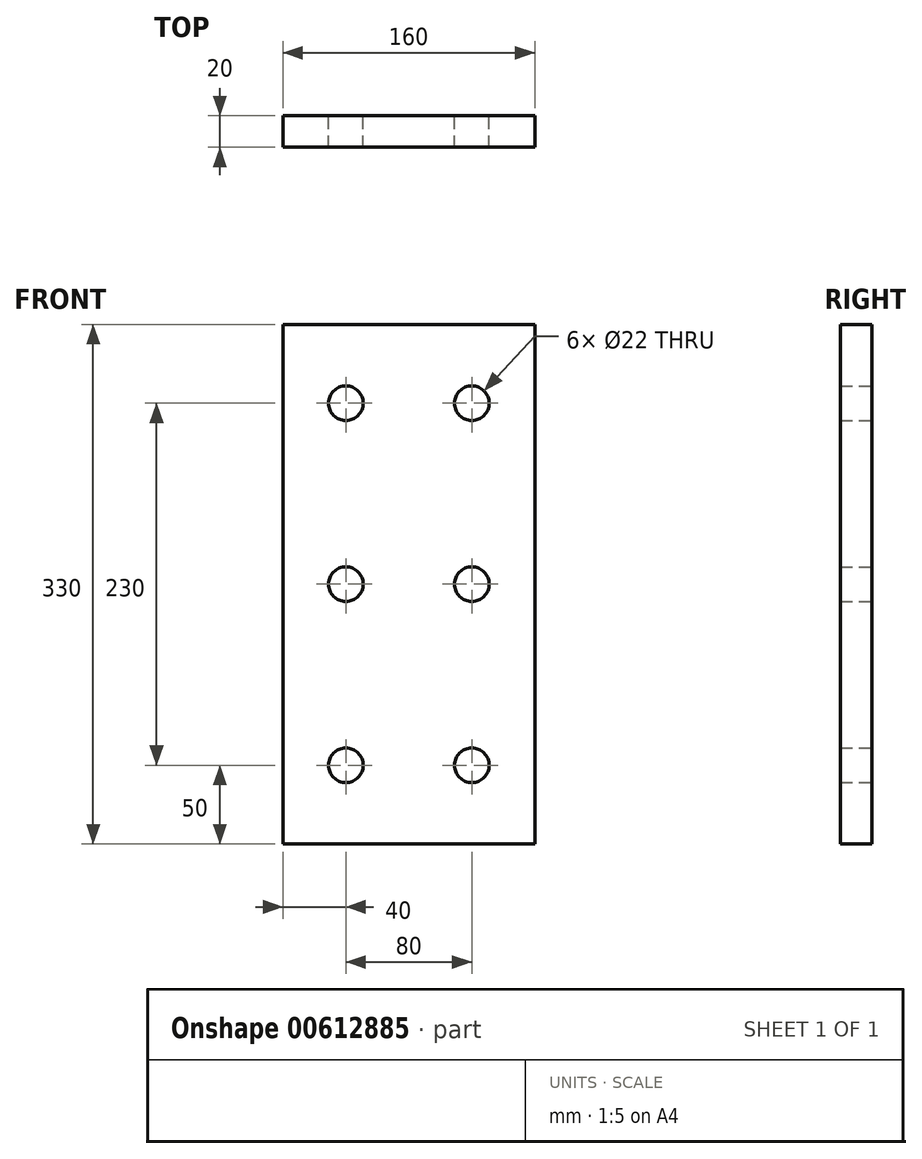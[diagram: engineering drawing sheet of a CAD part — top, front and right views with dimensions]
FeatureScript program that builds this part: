
annotation { "Feature Type Name" : "Feature", "Feature Type Description" : "" }
export const myFeature = defineFeature(function(context is Context, id is Id, definition is map)
    precondition{}
    {
        {
            var Q0;
            Q0=qCreatedBy(makeId("Front.planeOp"),FACE);
            var sketch = newSketch(context, id + "F0", { "sketchPlane" : qUnion([Q0])});
            skLineSegment(sketch, "E0.bottom", {"start": v(80, 165) * mm, "end": v(-80, 165) * mm});
            skLineSegment(sketch, "E0.top", {"start": v(80, -165) * mm, "end": v(-80, -165) * mm});
            skLineSegment(sketch, "E0.left", {"start": v(80, 165) * mm, "end": v(80, -165) * mm});
            skLineSegment(sketch, "E0.right", {"start": v(-80, 165) * mm, "end": v(-80, -165) * mm});
            skPoint(sketch, "E0.middle", {"position": v(0, 0) * mm});
            skCircle(sketch, "E1", {"center": v(-40, 115) * mm, "radius": 11 * mm});
            skCircle(sketch, "E2", {"center": v(40, 115) * mm, "radius": 11 * mm});
            skCircle(sketch, "E3", {"center": v(-40, -115) * mm, "radius": 11 * mm});
            skCircle(sketch, "E4", {"center": v(40, -115) * mm, "radius": 11 * mm});
            skCircle(sketch, "E5", {"center": v(-40, 0) * mm, "radius": 11 * mm});
            skCircle(sketch, "E6", {"center": v(40, 0) * mm, "radius": 11 * mm});
            skSolve(sketch);
        }
        {
            var Q0;
            Q0=makeQuery(id+"F0.imprint","IMPRINT",FACE,{"disambiguationData":[TD([[makeQuery(id+"F0.imprint","IMPRINT",EDGE,{"derivedFrom":sQuery(id+"F0.wireOp",EDGE,"E0.bottom")}),1.0]])]});
            extrude(context, id + "F1", {"entities" : qUnion([Q0]), "endBound" : BoundingType.SYMMETRIC, "depth" : 20 * mm, "offsetDistance" : 25 * mm});
        }
    });
